# Revit family: Specialty_Equipment-Planter-Planters_Unlimited-Marek-Round
name_source: partatom
category: Specialty Equipment
units: mm (PartAtom-declared; Revit-internal decimal feet)

## family parameters
Always vertical = Yes
Cut with Voids When Loaded = No
Enable Cutting in Views = Yes
Maintain Annotation Orientation = No
OmniClass Number = 23.40.05.21.17
OmniClass Title = Planters
Part Type = Normal
Room Calculation Point = No
Round Connector Dimension = Use Diameter
Shared = No
Work Plane-Based = No

## types (1)
- Default - Load Type Catalog
    Assembly Code = G2050600
    CD_Diameter = 18"
    CD_Diameter Max = 72"
    CD_Diameter Min = 18"
    CD_Height = 18"
    CD_Height Max = 60"
    CD_Height Min = 18"
    CD_Offset = 0"
    CD_Opening Diameter Bottom = 14 1/2"
    CD_Opening Diameter Top = 14"
    CD_Pads Offset = 4 13/32"
    CD_Pads Offset Radius = 6 1/4"
    CD_Product Name = Marek Planter
    CD_Product Page URL = https://www.plantersunlimited.com
    CD_Requested Diameter = 18"
    CD_Requested Height = 18"
    Default Elevation = 0"
    Description = Modular Planting Bed
    Manufacturer = Planters Unlimited
    Material = Plastic-Fiberglass-Carlsbad-Semi_Gloss-Charcoal
    Model = Marek Series Planters
    Type Comments = Round Planter
    URL = https://www.plantersunlimited.com

## geometry (parser evidence)
native form markers: Extrusion x1, Sweep x3
no freeform markers — native parametric forms only
